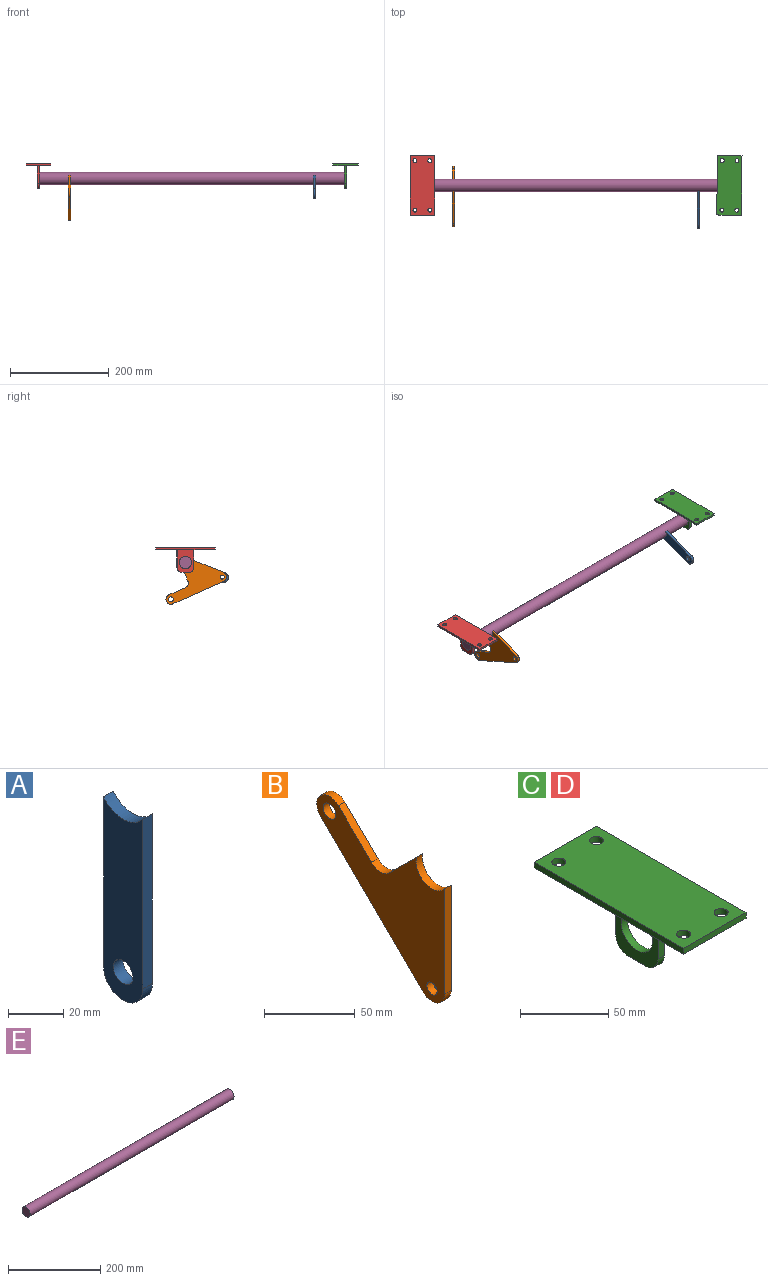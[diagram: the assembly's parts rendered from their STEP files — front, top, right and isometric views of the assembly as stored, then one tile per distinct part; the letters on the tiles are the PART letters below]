
ASSEMBLY  parts=5 mates=3
PART A: 7 faces, bbox 5x20x85 mm
  f0: cylinder r=12.5mm len=20mm, axis (-1,0,0), area 115.9mm2, adj f1,f3,f5,f6
  f1: plane 75x5mm, normal (0,-1,0), area 375mm2, adj f0,f2,f5,f6
  f2: cylinder r=10mm len=20mm, axis (-1,0,0), area 157.1mm2, adj f1,f3,f5,f6
  f3: plane 75x5mm, normal (0,1,0), area 375mm2, adj f0,f2,f5,f6
  f4: cylinder r=5mm len=10mm, axis (-1,0,0), area 157.1mm2, adj f5,f6
  f5: plane 85x20mm, normal (1,0,0), area 1508.6mm2, adj f0,f1,f2,f3,f4
  f6: plane 85x20mm, normal (-1,0,0), area 1508.6mm2, adj f0,f1,f2,f3,f4
PART B: 12 faces, bbox 5x100x98.6 mm
  f0: cylinder r=12.5mm len=22.5mm, axis (-1,0,0), area 169.4mm2, adj f1,f8,f10,f11
  f1: plane 71.1x5mm, normal (0,-1,0), area 355.5mm2, adj f0,f2,f10,f11
  f2: cylinder r=10mm len=17.01mm, axis (-1,0,0), area 117.4mm2, adj f1,f3,f10,f11
  f3: plane 80x78.6mm, normal (0,0.7,-0.71), area 560.8mm2, adj f2,f4,f10,f11
  f4: cylinder r=10mm len=17.13mm, axis (-1,0,0), area 157.1mm2, adj f3,f5,f10,f11
  f5: plane 25.85x25.4mm, normal (0,-0.7,0.71), area 181.2mm2, adj f4,f6,f10,f11
  f6: cylinder r=10mm len=14.08mm, axis (-1,0,0), area 78.1mm2, adj f5,f8,f10,f11
  f7: cylinder r=4mm len=8mm, axis (-1,0,0), area 125.7mm2, adj f10,f11
  f8: plane 20.84x20.84mm, normal (0,0.71,0.71), area 147.4mm2, adj f0,f6,f10,f11
  f9: cylinder r=5mm len=10mm, axis (-1,0,0), area 157.1mm2, adj f10,f11
  f10: plane 100x98.6mm, normal (1,0,0), area 4397.9mm2, adj f0,f1,f2,f3,f4,f5,f6,f7
  f11: plane 100x98.6mm, normal (-1,0,0), area 4397.9mm2, adj f0,f1,f2,f3,f4,f5,f6,f7
PART C: 18 faces, bbox 50x120x50 mm
  f0: plane 50x4mm, normal (0,1,0), area 200mm2, adj f1,f7,f8,f9
  f1: plane 120x4mm, normal (-1,0,0), area 480mm2, adj f0,f2,f8,f9
  f2: plane 50x4mm, normal (0,-1,0), area 200mm2, adj f1,f7,f8,f9
  f3: cylinder r=4mm len=8mm, axis (0,0,1), area 100.5mm2, adj f8,f9
  f4: cylinder r=4mm len=8mm, axis (0,0,1), area 100.5mm2, adj f8,f9
  f5: cylinder r=4mm len=8mm, axis (0,0,1), area 100.5mm2, adj f8,f9
  f6: cylinder r=4mm len=8mm, axis (0,0,1), area 100.5mm2, adj f8,f9
  f7: plane 120x4mm, normal (1,0,0), area 480mm2, adj f0,f2,f8,f9
  f8: plane 120x50mm, normal (0,0,-1), area 5628.9mm2, adj f0,f1,f2,f3,f4,f5,f6,f7
  f9: plane 120x50mm, normal (0,0,1), area 5798.9mm2, adj f0,f1,f2,f3,f4,f5,f6,f7
  f10: plane 14x5mm, normal (0,0,-1), area 70mm2, adj f12,f14,f15,f16
  f11: plane 36x5mm, normal (0,1,0), area 180mm2, adj f8,f12,f14,f16
  f12: plane 46x34mm, normal (1,0,0), area 1030.2mm2, adj f8,f10,f11,f13,f15,f16,f17
  f13: plane 36x5mm, normal (0,-1,0), area 180mm2, adj f8,f12,f14,f15
  f14: plane 46x34mm, normal (-1,0,0), area 1030.2mm2, adj f8,f10,f11,f13,f15,f16,f17
  f15: cylinder r=10mm len=10mm, axis (-1,0,0), area 78.5mm2, adj f10,f12,f13,f14
  f16: cylinder r=10mm len=10mm, axis (1,0,0), area 78.5mm2, adj f10,f11,f12,f14
  f17: cylinder r=12.5mm len=25mm, axis (-1,0,0), area 392.7mm2, adj f12,f14
PART D: same geometry as C
PART E: 3 faces, bbox 625x25x25 mm
  f0: cylinder r=12.5mm len=625mm, axis (-1,0,0), area 49087.4mm2, adj f1,f2
  f1: plane 25x25mm, normal (1,0,0), area 490.9mm2, adj f0
  f2: plane 25x25mm, normal (-1,0,0), area 490.9mm2, adj f0
PLACE A rot(axis=(-1,0,0),68.5deg) t=(655,-326.16,-485.01)mm
PLACE B rot(axis=(-1,0,0),68.5deg) t=(160,-143.73,-278.81)mm
PLACE C rot(axis=(0,0,-1),0.4deg) t=(1453.17,136.36,-125.65)mm
PLACE D rot(axis=(0.9,0.04,-0.44),0deg) t=(830.19,141,-125.65)mm
PLACE E rot(axis=(-1,0,0),158.5deg) t=(97.5,-753.79,-402.31)mm
MATE revolute D.f17 <-> E.f0  axis (-1,0,0) through (97.5,-272.02,-155.65)mm
MATE fastened E.f0 <-> B.f0  axis (-1,0,0) through (722.5,-272.02,-155.65)mm
MATE fastened E.f0 <-> A.f0  axis (-1,0,0) through (722.5,-272.02,-155.65)mm
